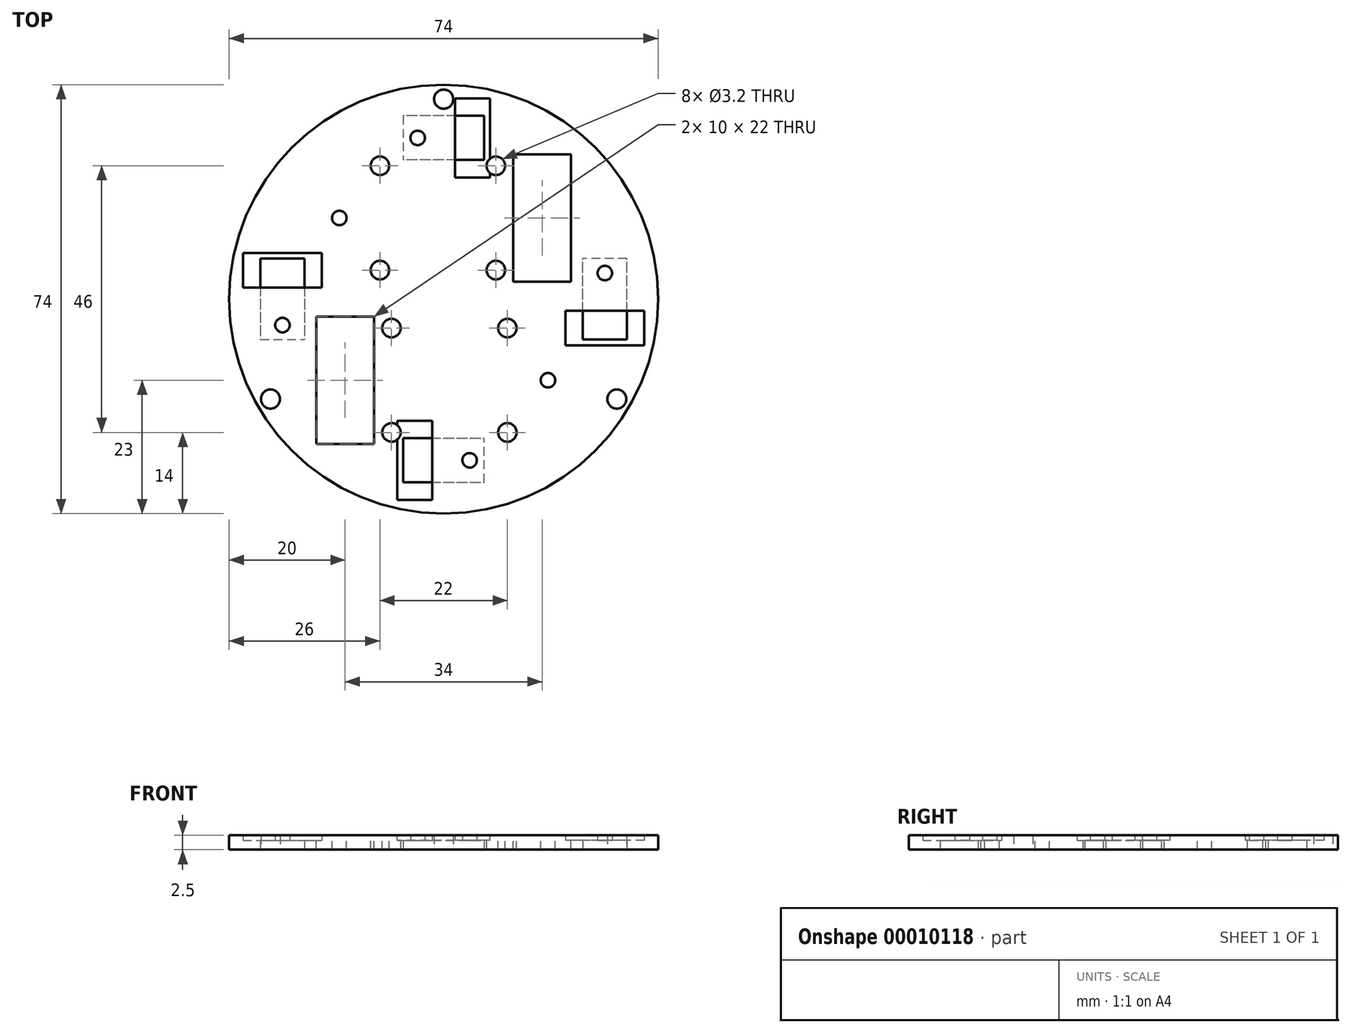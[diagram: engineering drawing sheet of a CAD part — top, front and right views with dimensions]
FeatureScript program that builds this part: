
annotation { "Feature Type Name" : "Feature", "Feature Type Description" : "" }
export const myFeature = defineFeature(function(context is Context, id is Id, definition is map)
    precondition{}
    {
        {
            var Q0;
            Q0=qCreatedBy(makeId("Top.planeOp"),FACE);
            var sketch = newSketch(context, id + "F0", { "sketchPlane" : qUnion([Q0])});
            skCircle(sketch, "E0", {"center": v(0, 0) * mm, "radius": 37 * mm});
            skCircle(sketch, "E1", {"center": v(0, 34.5) * mm, "radius": 1.65 * mm});
            skLineSegment(sketch, "E2", {"start": v(0, 0) * mm, "end": v(0, 34.5) * mm});
            skCircle(sketch, "E3.1.0", {"center": v(-29.88, -17.25) * mm, "radius": 1.65 * mm});
            skCircle(sketch, "E3.2.0", {"center": v(29.88, -17.25) * mm, "radius": 1.65 * mm});
            skSolve(sketch);
        }
        {
            var Q0;
            Q0 = qSketchRegion(id + "F0", true);
            extrude(context, id + "F1", {"entities" : qUnion([Q0]), "depth" : 2.5 * mm});
        }
        {
            var Q0;
            Q0=makeQuery(id+"F1.opExtrude","CAP_FACE",FACE,{"disambiguationData":[OSD([sQuery(id+"F0.wireOp",EDGE,"E0"),sQuery(id+"F0.wireOp",EDGE,"E1"),sQuery(id+"F0.wireOp",EDGE,"E3.1.0"),sQuery(id+"F0.wireOp",EDGE,"E3.2.0")])],"isStart":false});
            var sketch = newSketch(context, id + "F2", { "sketchPlane" : qUnion([Q0])});
            skLineSegment(sketch, "E4.top", {"start": v(-22, -25) * mm, "end": v(-12, -25) * mm});
            skLineSegment(sketch, "E4.right", {"start": v(-22, -3) * mm, "end": v(-22, -25) * mm});
            skLineSegment(sketch, "E5.bottom", {"start": v(-12, -20) * mm, "end": v(14, -20) * mm, "construction": true});
            skLineSegment(sketch, "E5.top", {"start": v(-22, -8) * mm, "end": v(14, -8) * mm, "construction": true});
            skLineSegment(sketch, "E5.right", {"start": v(14, -20) * mm, "end": v(14, -8) * mm, "construction": true});
            skLineSegment(sketch, "E6", {"start": v(-22, -8) * mm, "end": v(-22, -7) * mm, "construction": true});
            skLineSegment(sketch, "E7", {"start": v(-22, -7) * mm, "end": v(14, -7) * mm, "construction": true});
            skLineSegment(sketch, "E8", {"start": v(14, -7) * mm, "end": v(14, -8) * mm, "construction": true});
            skLineSegment(sketch, "E9", {"start": v(-4, -7) * mm, "end": v(-4, 0) * mm, "construction": true});
            skLineSegment(sketch, "E10", {"start": v(-4, 0) * mm, "end": v(0, 0) * mm, "construction": true});
            skLineSegment(sketch, "E11", {"start": v(14, -14) * mm, "end": v(18, -14) * mm});
            skCircle(sketch, "E12", {"center": v(18, -14) * mm, "radius": 1.25 * mm});
            skCircle(sketch, "E13", {"center": v(-9, -23) * mm, "radius": 1.6 * mm});
            skCircle(sketch, "E14", {"center": v(11, -23) * mm, "radius": 1.6 * mm});
            skLineSegment(sketch, "E15", {"start": v(-9, -23) * mm, "end": v(11, -23) * mm, "construction": true});
            skLineSegment(sketch, "E16", {"start": v(1, -23) * mm, "end": v(1, -20) * mm, "construction": true});
            skLineSegment(sketch, "E17", {"start": v(-12, -14) * mm, "end": v(14, -14) * mm, "construction": true});
            skCircle(sketch, "E18.0.MirrorC", {"center": v(11, -5) * mm, "radius": 1.6 * mm});
            skCircle(sketch, "E18.1.MirrorC", {"center": v(-9, -5) * mm, "radius": 1.6 * mm});
            skPoint(sketch, "E19.center", {"position": v(0, 0) * mm});
            skLineSegment(sketch, "E20", {"start": v(-22, -3) * mm, "end": v(-12, -3) * mm});
            skLineSegment(sketch, "E21", {"start": v(-12, -25) * mm, "end": v(-12, -20) * mm});
            skLineSegment(sketch, "E22", {"start": v(-12, -20) * mm, "end": v(-12, -14) * mm});
            skLineSegment(sketch, "E23", {"start": v(-12, -14) * mm, "end": v(-12, -8) * mm});
            skLineSegment(sketch, "E24", {"start": v(-12, -8) * mm, "end": v(-12, -3) * mm});
            skLineSegment(sketch, "E25.1.0", {"start": v(22, 3) * mm, "end": v(12, 3) * mm});
            skLineSegment(sketch, "E25.1.1", {"start": v(22, 3) * mm, "end": v(22, 25) * mm});
            skLineSegment(sketch, "E25.1.2", {"start": v(22, 25) * mm, "end": v(12, 25) * mm});
            skLineSegment(sketch, "E25.1.3", {"start": v(12, 25) * mm, "end": v(12, 20) * mm});
            skLineSegment(sketch, "E25.1.4", {"start": v(12, 20) * mm, "end": v(12, 14) * mm});
            skLineSegment(sketch, "E25.1.5", {"start": v(12, 14) * mm, "end": v(12, 8) * mm});
            skLineSegment(sketch, "E25.1.6", {"start": v(12, 8) * mm, "end": v(12, 3) * mm});
            skCircle(sketch, "E25.1.7", {"center": v(9, 5) * mm, "radius": 1.6 * mm});
            skCircle(sketch, "E25.1.8", {"center": v(-11, 5) * mm, "radius": 1.6 * mm});
            skCircle(sketch, "E25.1.9", {"center": v(-18, 14) * mm, "radius": 1.25 * mm});
            skCircle(sketch, "E25.1.10", {"center": v(-11, 23) * mm, "radius": 1.6 * mm});
            skCircle(sketch, "E25.1.11", {"center": v(9, 23) * mm, "radius": 1.6 * mm});
            skSolve(sketch);
        }
        {
            var Q0;
            Q0 = qSketchRegion(id + "F2", true);
            extrude(context, id + "F3", {"entities" : qUnion([Q0]), "operationType" : NewBodyOperationType.REMOVE, "endBound" : BoundingType.UP_TO_NEXT, "oppositeDirection" : true, "depth" : 25 * mm});
        }
        {
            var Q0;
            Q0=makeQuery(id+"F1.opExtrude","CAP_FACE",FACE,{"disambiguationData":[OSD([sQuery(id+"F0.wireOp",EDGE,"E0"),sQuery(id+"F0.wireOp",EDGE,"E1"),sQuery(id+"F0.wireOp",EDGE,"E3.1.0"),sQuery(id+"F0.wireOp",EDGE,"E3.2.0")])],"isStart":true});
            var sketch = newSketch(context, id + "F4", { "sketchPlane" : qUnion([Q0])});
            skLineSegment(sketch, "E26.bottom", {"start": v(-6.99, 31.62) * mm, "end": v(6.98, 31.62) * mm});
            skLineSegment(sketch, "E26.top", {"start": v(-6.98, 24) * mm, "end": v(6.98, 24) * mm});
            skLineSegment(sketch, "E26.left", {"start": v(-6.99, 31.62) * mm, "end": v(-6.99, 24) * mm});
            skLineSegment(sketch, "E26.right", {"start": v(6.98, 31.62) * mm, "end": v(6.98, 24) * mm});
            skLineSegment(sketch, "E27", {"start": v(0, 0) * mm, "end": v(0, 24) * mm, "construction": true});
            skLineSegment(sketch, "E28.1.0", {"start": v(-31.62, -6.98) * mm, "end": v(-31.62, 6.98) * mm});
            skLineSegment(sketch, "E28.1.1", {"start": v(-31.62, -6.99) * mm, "end": v(-24, -6.99) * mm});
            skLineSegment(sketch, "E28.1.2", {"start": v(-24, -6.98) * mm, "end": v(-24, 6.98) * mm});
            skLineSegment(sketch, "E28.1.3", {"start": v(-31.62, 6.98) * mm, "end": v(-24, 6.98) * mm});
            skLineSegment(sketch, "E28.2.0", {"start": v(6.98, -31.62) * mm, "end": v(-6.99, -31.62) * mm});
            skLineSegment(sketch, "E28.2.1", {"start": v(6.99, -31.62) * mm, "end": v(6.99, -24) * mm});
            skLineSegment(sketch, "E28.2.2", {"start": v(6.98, -24) * mm, "end": v(-6.98, -24) * mm});
            skLineSegment(sketch, "E28.2.3", {"start": v(-6.98, -31.62) * mm, "end": v(-6.98, -24) * mm});
            skLineSegment(sketch, "E28.3.0", {"start": v(31.62, 6.99) * mm, "end": v(31.62, -6.98) * mm});
            skLineSegment(sketch, "E28.3.1", {"start": v(31.62, 6.99) * mm, "end": v(24, 6.99) * mm});
            skLineSegment(sketch, "E28.3.2", {"start": v(24, 6.98) * mm, "end": v(24, -6.98) * mm});
            skLineSegment(sketch, "E28.3.3", {"start": v(31.62, -6.98) * mm, "end": v(24, -6.98) * mm});
            skPoint(sketch, "E28.center", {"position": v(0, 0) * mm});
            skSolve(sketch);
        }
        {
            var Q0;
            Q0 = qSketchRegion(id + "F4", true);
            extrude(context, id + "F5", {"entities" : qUnion([Q0]), "operationType" : NewBodyOperationType.REMOVE, "oppositeDirection" : true, "depth" : 1.6 * mm});
        }
        {
            var Q0;
            Q0=makeQuery(id+"F5.boolean.opBoolean","COPY",FACE,{"derivedFrom":makeQuery(id+"F5.opExtrude","CAP_FACE",FACE,{"disambiguationData":[OSD([sQuery(id+"F4.wireOp",EDGE,"E26.bottom"),sQuery(id+"F4.wireOp",EDGE,"E26.top"),sQuery(id+"F4.wireOp",EDGE,"E26.left"),sQuery(id+"F4.wireOp",EDGE,"E26.right")])],"isStart":false})});
            var sketch = newSketch(context, id + "F6", { "sketchPlane" : qUnion([Q0])});
            skLineSegment(sketch, "E29", {"start": v(6.98, 27.81) * mm, "end": v(4.48, 27.81) * mm});
            skLineSegment(sketch, "E30.bottom", {"start": v(-7.99, 34.62) * mm, "end": v(-1.99, 34.62) * mm});
            skLineSegment(sketch, "E30.top", {"start": v(-7.99, 21) * mm, "end": v(-1.99, 21) * mm});
            skLineSegment(sketch, "E30.left", {"start": v(-7.99, 34.62) * mm, "end": v(-7.99, 21) * mm});
            skLineSegment(sketch, "E30.right", {"start": v(-1.99, 34.62) * mm, "end": v(-1.99, 21) * mm});
            skCircle(sketch, "E31", {"center": v(4.48, 27.81) * mm, "radius": 1.25 * mm});
            skLineSegment(sketch, "E32.1.0", {"start": v(-34.62, -7.99) * mm, "end": v(-34.62, -1.99) * mm});
            skLineSegment(sketch, "E32.1.1", {"start": v(-34.62, -7.99) * mm, "end": v(-21, -7.98) * mm});
            skLineSegment(sketch, "E32.1.2", {"start": v(-21, -7.99) * mm, "end": v(-21, -1.99) * mm});
            skLineSegment(sketch, "E32.1.3", {"start": v(-34.62, -1.99) * mm, "end": v(-21, -1.98) * mm});
            skCircle(sketch, "E32.1.4", {"center": v(-27.81, 4.48) * mm, "radius": 1.25 * mm});
            skLineSegment(sketch, "E32.2.0", {"start": v(7.98, -34.62) * mm, "end": v(1.98, -34.62) * mm});
            skLineSegment(sketch, "E32.2.1", {"start": v(7.99, -34.62) * mm, "end": v(7.98, -21) * mm});
            skLineSegment(sketch, "E32.2.2", {"start": v(7.99, -21) * mm, "end": v(1.98, -21) * mm});
            skLineSegment(sketch, "E32.2.3", {"start": v(1.99, -34.62) * mm, "end": v(1.98, -21) * mm});
            skCircle(sketch, "E32.2.4", {"center": v(-4.48, -27.81) * mm, "radius": 1.25 * mm});
            skLineSegment(sketch, "E32.3.0", {"start": v(34.62, 7.99) * mm, "end": v(34.62, 1.99) * mm});
            skLineSegment(sketch, "E32.3.1", {"start": v(34.62, 7.99) * mm, "end": v(21, 7.99) * mm});
            skLineSegment(sketch, "E32.3.2", {"start": v(21, 7.99) * mm, "end": v(21, 1.99) * mm});
            skLineSegment(sketch, "E32.3.3", {"start": v(34.62, 1.99) * mm, "end": v(21, 1.99) * mm});
            skCircle(sketch, "E32.3.4", {"center": v(27.81, -4.48) * mm, "radius": 1.25 * mm});
            skPoint(sketch, "E32.center", {"position": v(0, 0) * mm});
            skSolve(sketch);
        }
        {
            var Q0;
            Q0 = qSketchRegion(id + "F6", true);
            extrude(context, id + "F7", {"entities" : qUnion([Q0]), "operationType" : NewBodyOperationType.REMOVE, "endBound" : BoundingType.UP_TO_NEXT, "oppositeDirection" : true, "depth" : 25 * mm});
        }
    });
